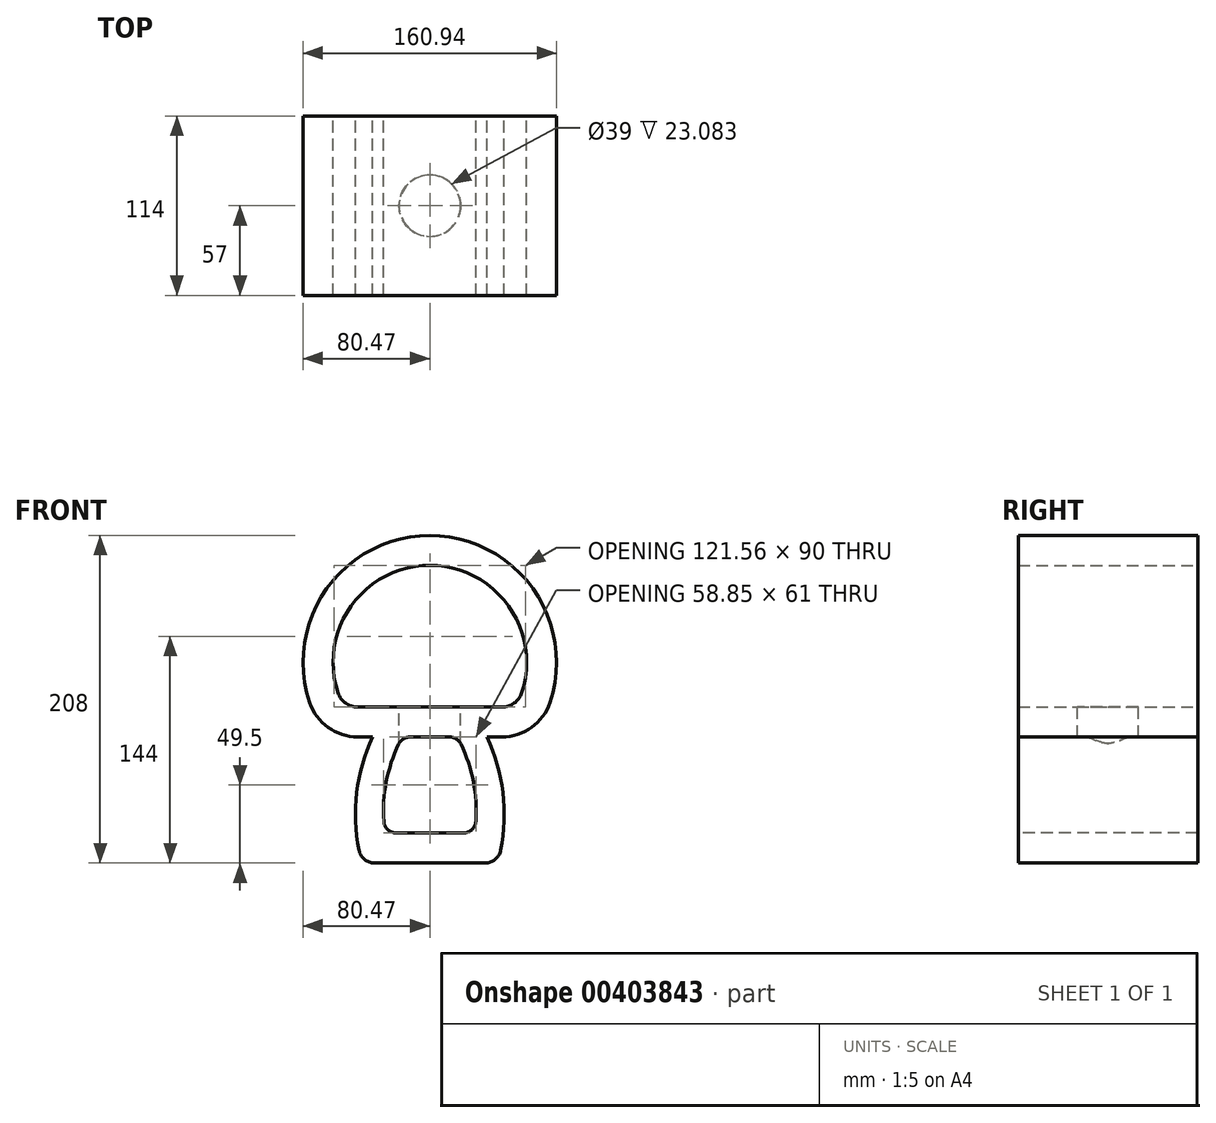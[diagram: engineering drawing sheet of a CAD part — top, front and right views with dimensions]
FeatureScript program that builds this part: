
annotation { "Feature Type Name" : "Feature", "Feature Type Description" : "" }
export const myFeature = defineFeature(function(context is Context, id is Id, definition is map)
    precondition{}
    {
        {
            var Q0;
            Q0=qCreatedBy(makeId("Front.planeOp"),FACE);
            var sketch = newSketch(context, id + "F0", { "sketchPlane" : qUnion([Q0])});
            skArc(sketch, "E0", {"start": v(-17.4, 76) * mm, "mid": v(-27.88, 46.4) * mm, "end": v(-28.4, 15) * mm});
            skArc(sketch, "E1.1", {"start": v(-58.3, 104.01) * mm, "mid": v(-53.49, 97.49) * mm, "end": v(-45.77, 95) * mm});
            skArc(sketch, "E1.2", {"start": v(0, 185) * mm, "mid": v(-49.9, 159.44) * mm, "end": v(-58.3, 104.01) * mm});
            skArc(sketch, "E2.MirrorCS", {"start": v(17.4, 76) * mm, "mid": v(27.88, 46.4) * mm, "end": v(28.4, 15) * mm});
            skArc(sketch, "E3.MirrorCS", {"start": v(58.3, 104.01) * mm, "mid": v(53.49, 97.49) * mm, "end": v(45.77, 95) * mm});
            skArc(sketch, "E4.MirrorCS", {"start": v(0, 185) * mm, "mid": v(49.9, 159.44) * mm, "end": v(58.3, 104.01) * mm});
            skLineSegment(sketch, "E5", {"start": v(-45.77, 95) * mm, "end": v(45.77, 95) * mm});
            skLineSegment(sketch, "E6", {"start": v(-17.4, 76) * mm, "end": v(17.4, 76) * mm});
            skLineSegment(sketch, "E7", {"start": v(-28.4, 15) * mm, "end": v(28.4, 15) * mm});
            skArc(sketch, "E8.0", {"start": v(0, 204) * mm, "mid": v(65.31, 170.54) * mm, "end": v(76.31, 97.98) * mm});
            skArc(sketch, "E8.1", {"start": v(76.31, 97.98) * mm, "mid": v(64.59, 82.07) * mm, "end": v(45.77, 76) * mm});
            skArc(sketch, "E8.2", {"start": v(0, 204) * mm, "mid": v(-65.31, 170.54) * mm, "end": v(-76.31, 97.98) * mm});
            skLineSegment(sketch, "E8.3", {"start": v(36.44, 76) * mm, "end": v(45.77, 76) * mm});
            skArc(sketch, "E8.4", {"start": v(36.44, 76) * mm, "mid": v(46.8, 36.59) * mm, "end": v(43.1, -4) * mm});
            skArc(sketch, "E8.5", {"start": v(-76.31, 97.98) * mm, "mid": v(-64.59, 82.07) * mm, "end": v(-45.77, 76) * mm});
            skLineSegment(sketch, "E8.6", {"start": v(-36.44, 76) * mm, "end": v(-45.77, 76) * mm});
            skArc(sketch, "E8.7", {"start": v(-36.44, 76) * mm, "mid": v(-46.8, 36.59) * mm, "end": v(-43.1, -4) * mm});
            skLineSegment(sketch, "E8.8", {"start": v(-43.1, -4) * mm, "end": v(43.1, -4) * mm});
            skSolve(sketch);
        }
        {
            var Q0;
            Q0 = qSketchRegion(id + "F0", true);
            extrude(context, id + "F1", {"entities" : qUnion([Q0]), "endBound" : BoundingType.SYMMETRIC, "depth" : 114 * mm});
        }
        {
            var Q0;
            Q0=makeQuery(id+"F1.opExtrude","SWEPT_EDGE",EDGE,{"disambiguationData":[OSD([sQuery(id+"F0.wireOp",EDGE,"E8.7"),sQuery(id+"F0.wireOp",EDGE,"E8.8")])]});
            var Q1;
            Q1=makeQuery(id+"F1.opExtrude","SWEPT_EDGE",EDGE,{"disambiguationData":[OSD([sQuery(id+"F0.wireOp",EDGE,"E8.4"),sQuery(id+"F0.wireOp",EDGE,"E8.8")])]});
            fillet(context, id + "F2", {"entities" : qUnion([Q0, Q1]), "radius" : 10 * mm, "tangentPropagation" : true, "allowEdgeOverflow" : false});
        }
        {
            var Q0;
            Q0=makeQuery(id+"F1.opExtrude","SWEPT_EDGE",EDGE,{"disambiguationData":[OSD([sQuery(id+"F0.wireOp",EDGE,"E0"),sQuery(id+"F0.wireOp",EDGE,"E6")])]});
            var Q1;
            Q1=makeQuery(id+"F1.opExtrude","SWEPT_EDGE",EDGE,{"disambiguationData":[OSD([sQuery(id+"F0.wireOp",EDGE,"E2.MirrorCS"),sQuery(id+"F0.wireOp",EDGE,"E6")])]});
            var Q2;
            Q2=makeQuery(id+"F1.opExtrude","SWEPT_EDGE",EDGE,{"disambiguationData":[OSD([sQuery(id+"F0.wireOp",EDGE,"E2.MirrorCS"),sQuery(id+"F0.wireOp",EDGE,"E7")])]});
            var Q3;
            {var subQ0=sQuery(id+"F0.wireOp",EDGE,"E8.8");Q3=makeQuery(id+"F2.opFillet","BLEND_EDGE",EDGE,{"blendedFrom":[makeQuery(id+"F1.opExtrude","SWEPT_EDGE",EDGE,{"disambiguationData":[OSD([sQuery(id+"F0.wireOp",EDGE,"E8.4"),subQ0])]}),makeQuery(id+"F1.opExtrude","SWEPT_FACE",FACE,{"disambiguationData":[OSD([subQ0])]})],"blendedInto":[makeQuery(id+"F1.opExtrude","SWEPT_FACE",FACE,{"disambiguationData":[OSD([subQ0])]})]});}
            var Q4;
            Q4=makeQuery(id+"F1.opExtrude","SWEPT_EDGE",EDGE,{"disambiguationData":[OSD([sQuery(id+"F0.wireOp",EDGE,"E0"),sQuery(id+"F0.wireOp",EDGE,"E7")])]});
            fillet(context, id + "F3", {"entities" : qUnion([Q0, Q1, Q2, Q3, Q4]), "radius" : 8 * mm, "tangentPropagation" : true, "allowEdgeOverflow" : false});
        }
        {
            var Q0;
            Q0=makeQuery(id+"F1.opExtrude","SWEPT_FACE",FACE,{"disambiguationData":[OSD([sQuery(id+"F0.wireOp",EDGE,"E5")])]});
            var sketch = newSketch(context, id + "F4", { "sketchPlane" : qUnion([Q0])});
            skCircle(sketch, "E9", {"center": v(0, 0) * mm, "radius": 19.5 * mm});
            skSolve(sketch);
        }
        {
            var Q0;
            Q0=makeQuery(id+"F4.imprint","IMPRINT",FACE,{"disambiguationData":[TD([[makeQuery(id+"F4.imprint","IMPRINT",EDGE,{"derivedFrom":sQuery(id+"F4.wireOp",EDGE,"E9")}),1.0]])]});
            extrude(context, id + "F5", {"entities" : qUnion([Q0]), "operationType" : NewBodyOperationType.REMOVE, "endBound" : BoundingType.UP_TO_NEXT, "oppositeDirection" : true, "depth" : 25 * mm});
        }
    });
